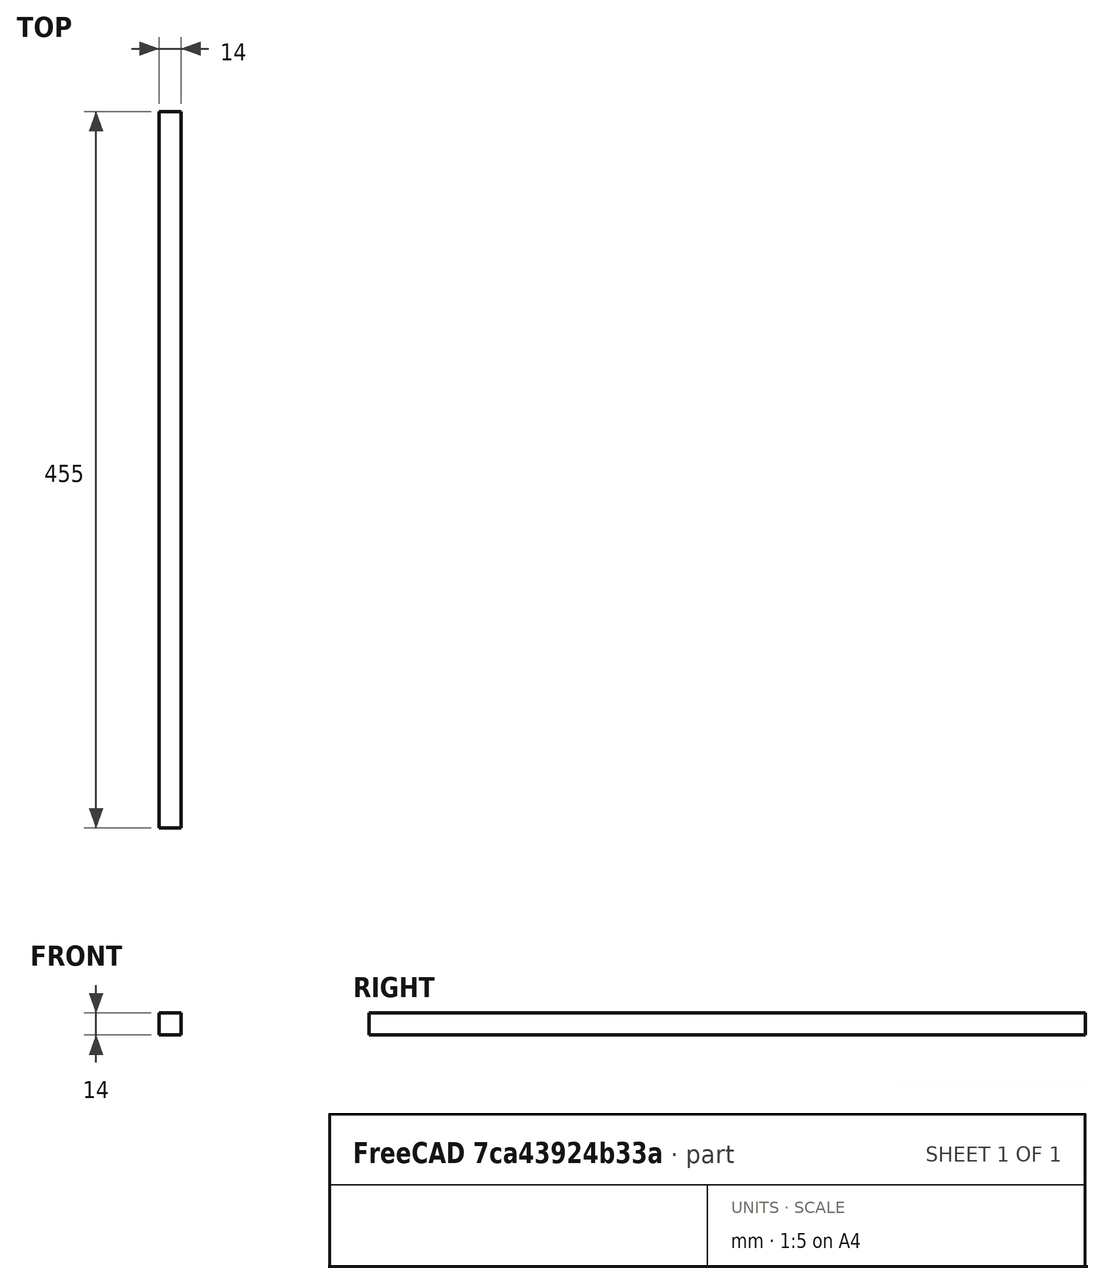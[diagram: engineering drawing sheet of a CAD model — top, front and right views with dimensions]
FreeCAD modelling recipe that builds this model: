
FCSTD DOCUMENT  (FreeCAD 0.19R24276 (Git))
Label: 3000_strut_x_14_14_455
License: All rights reserved
LicenseURL: http://en.wikipedia.org/wiki/All_rights_reserved
objects: Spreadsheet::Sheet×1, Sketcher::SketchObject×1, PartDesign::Pad×1, PartDesign::Body×1
note: 4 computed .brp shape members not serialized (recipe doc carries the construction recipe); baked Part::Feature solids carry a one-line shape summary decoded from their .brp

FEATURE [Spreadsheet::Sheet] Spreadsheet  label="xls"
  cells = B5=STRUT ; C5=14 X 14 mm; B6= width 1; C6=w1; D6(w1)=14; E6=mm; B7=Width 2; C7=w2; D7(w2)=14; E7=mm
FEATURE [Sketcher::SketchObject] Sketch
  FullyConstrained = true
  MapMode = 5
  Placement = pos=(0,0,0) rot=(1,0,0;1.5708rad)
  Support = -> [XZ_Plane]
  expr: Constraints[10] = <<xls>>.w2
  expr: Constraints[9] = <<xls>>.w1
  sketch-geometry (4):
    g0: LineSegment StartX=0 StartY=0 StartZ=0 EndX=14 EndY=0 EndZ=0
    g1: LineSegment StartX=14 StartY=0 StartZ=0 EndX=14 EndY=14 EndZ=0
    g2: LineSegment StartX=14 StartY=14 StartZ=0 EndX=0 EndY=14 EndZ=0
    g3: LineSegment StartX=0 StartY=14 StartZ=0 EndX=0 EndY=0 EndZ=0
  constraints (11):
    c: Coincident(g0,g1)
    c: Coincident(g1,g2)
    c: Coincident(g2,g3)
    c: Coincident(g3,g0)
    c: Horizontal(g0)
    c: Horizontal(g2)
    c: Vertical(g1)
    c: Vertical(g3)
    c: Coincident(g0,g-1)
    c: DistanceX(g2,g2) = 14
    c: DistanceY(g1,g1) = 14
FEATURE [PartDesign::Pad] Pad
  Direction = (1,1,1)
  Length = 455
  Length2 = 100
  Placement = pos=(0,0,0) rot=(1,0,0;1.5708rad)
  Profile = -> Sketch
  Reversed = true
  Type = 0
FEATURE [PartDesign::Body] Body
  Group = -> [Sketch,Pad]
  Origin = -> Origin
  Tip = -> Pad
